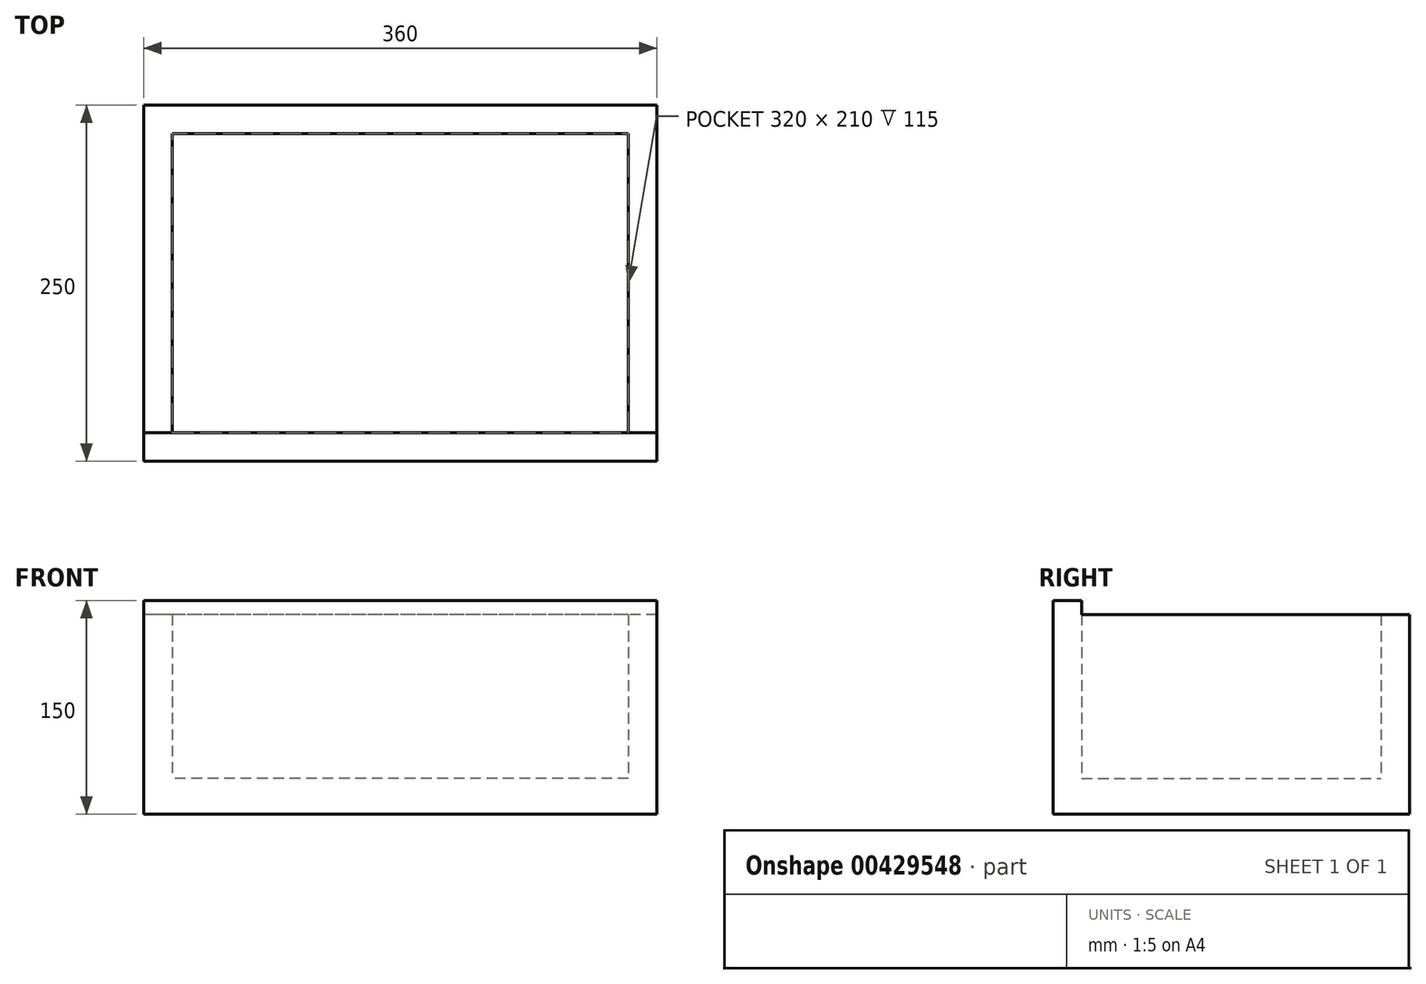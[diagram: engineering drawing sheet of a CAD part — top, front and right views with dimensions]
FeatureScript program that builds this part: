
annotation { "Feature Type Name" : "Feature", "Feature Type Description" : "" }
export const myFeature = defineFeature(function(context is Context, id is Id, definition is map)
    precondition{}
    {
        {
            var Q0;
            Q0=qCreatedBy(makeId("Top.planeOp"),FACE);
            var sketch = newSketch(context, id + "F0", { "sketchPlane" : qUnion([Q0])});
            skLineSegment(sketch, "E0.bottom", {"start": v(180, -125) * mm, "end": v(-180, -125) * mm});
            skLineSegment(sketch, "E0.top", {"start": v(180, 125) * mm, "end": v(-180, 125) * mm});
            skLineSegment(sketch, "E0.left", {"start": v(180, -125) * mm, "end": v(180, 125) * mm});
            skLineSegment(sketch, "E0.right", {"start": v(-180, -125) * mm, "end": v(-180, 125) * mm});
            skPoint(sketch, "E0.middle", {"position": v(0, 0) * mm});
            skLineSegment(sketch, "E1.0", {"start": v(160, -125) * mm, "end": v(160, 125) * mm});
            skLineSegment(sketch, "E2.0", {"start": v(180, 105) * mm, "end": v(-180, 105) * mm});
            skLineSegment(sketch, "E3.0", {"start": v(-160, -125) * mm, "end": v(-160, 125) * mm});
            skLineSegment(sketch, "E4.0", {"start": v(180, -105) * mm, "end": v(-180, -105) * mm});
            skSolve(sketch);
        }
        {
            var Q0;
            {var subQ0=sQuery(id+"F0.wireOp",EDGE,"E0.right");var subQ1=sQuery(id+"F0.wireOp",EDGE,"E0.bottom");var subQ2=makeQuery(id+"F0.imprint","INTERSECT",VERTEX,{"derivedFrom":[subQ1,subQ0]});Q0=makeQuery(id+"F0.imprint","IMPRINT",FACE,{"disambiguationData":[TD([[makeQuery(id+"F0.imprint","IMPRINT",EDGE,{"disambiguationData":[TD([[subQ2,1.0]])],"derivedFrom":subQ1}),-1.0]])]});}
            var Q1;
            {var subQ0=sQuery(id+"F0.wireOp",EDGE,"E1.0");var subQ1=sQuery(id+"F0.wireOp",EDGE,"E0.bottom");var subQ2=makeQuery(id+"F0.imprint","INTERSECT",VERTEX,{"derivedFrom":[subQ1,subQ0]});Q1=makeQuery(id+"F0.imprint","IMPRINT",FACE,{"disambiguationData":[TD([[makeQuery(id+"F0.imprint","IMPRINT",EDGE,{"disambiguationData":[TD([[subQ2,-1.0]])],"derivedFrom":subQ1}),-1.0]])]});}
            var Q2;
            {var subQ0=sQuery(id+"F0.wireOp",EDGE,"E0.left");var subQ1=sQuery(id+"F0.wireOp",EDGE,"E0.bottom");var subQ2=makeQuery(id+"F0.imprint","INTERSECT",VERTEX,{"derivedFrom":[subQ1,subQ0]});Q2=makeQuery(id+"F0.imprint","IMPRINT",FACE,{"disambiguationData":[TD([[makeQuery(id+"F0.imprint","IMPRINT",EDGE,{"disambiguationData":[TD([[subQ2,-1.0]])],"derivedFrom":subQ1}),-1.0]])]});}
            extrude(context, id + "F1", {"entities" : qUnion([Q0, Q1, Q2]), "depth" : 150 * mm});
        }
        {
            var Q0;
            {var subQ0=sQuery(id+"F0.wireOp",EDGE,"E2.0");var subQ1=sQuery(id+"F0.wireOp",EDGE,"E0.right");var subQ2=makeQuery(id+"F0.imprint","INTERSECT",VERTEX,{"derivedFrom":[subQ1,subQ0]});Q0=makeQuery(id+"F0.imprint","IMPRINT",FACE,{"disambiguationData":[TD([[makeQuery(id+"F0.imprint","IMPRINT",EDGE,{"disambiguationData":[TD([[subQ2,1.0]])],"derivedFrom":subQ1}),-1.0]])]});}
            var Q1;
            {var subQ0=sQuery(id+"F0.wireOp",EDGE,"E0.right");var subQ1=sQuery(id+"F0.wireOp",EDGE,"E0.top");var subQ2=makeQuery(id+"F0.imprint","INTERSECT",VERTEX,{"derivedFrom":[subQ1,subQ0]});Q1=makeQuery(id+"F0.imprint","IMPRINT",FACE,{"disambiguationData":[TD([[makeQuery(id+"F0.imprint","IMPRINT",EDGE,{"disambiguationData":[TD([[subQ2,1.0]])],"derivedFrom":subQ1}),1.0]])]});}
            var Q2;
            {var subQ0=sQuery(id+"F0.wireOp",EDGE,"E1.0");var subQ1=sQuery(id+"F0.wireOp",EDGE,"E0.top");var subQ2=makeQuery(id+"F0.imprint","INTERSECT",VERTEX,{"derivedFrom":[subQ1,subQ0]});Q2=makeQuery(id+"F0.imprint","IMPRINT",FACE,{"disambiguationData":[TD([[makeQuery(id+"F0.imprint","IMPRINT",EDGE,{"disambiguationData":[TD([[subQ2,-1.0]])],"derivedFrom":subQ1}),1.0]])]});}
            var Q3;
            {var subQ0=sQuery(id+"F0.wireOp",EDGE,"E0.left");var subQ1=sQuery(id+"F0.wireOp",EDGE,"E0.top");var subQ2=makeQuery(id+"F0.imprint","INTERSECT",VERTEX,{"derivedFrom":[subQ1,subQ0]});Q3=makeQuery(id+"F0.imprint","IMPRINT",FACE,{"disambiguationData":[TD([[makeQuery(id+"F0.imprint","IMPRINT",EDGE,{"disambiguationData":[TD([[subQ2,-1.0]])],"derivedFrom":subQ1}),1.0]])]});}
            var Q4;
            {var subQ0=sQuery(id+"F0.wireOp",EDGE,"E2.0");var subQ1=sQuery(id+"F0.wireOp",EDGE,"E0.left");var subQ2=makeQuery(id+"F0.imprint","INTERSECT",VERTEX,{"derivedFrom":[subQ1,subQ0]});Q4=makeQuery(id+"F0.imprint","IMPRINT",FACE,{"disambiguationData":[TD([[makeQuery(id+"F0.imprint","IMPRINT",EDGE,{"disambiguationData":[TD([[subQ2,1.0]])],"derivedFrom":subQ1}),1.0]])]});}
            extrude(context, id + "F2", {"entities" : qUnion([Q0, Q1, Q2, Q3, Q4]), "operationType" : NewBodyOperationType.ADD, "depth" : 140 * mm});
        }
        {
            var Q0;
            {var subQ0=sQuery(id+"F0.wireOp",EDGE,"E4.0");var subQ1=sQuery(id+"F0.wireOp",EDGE,"E1.0");var subQ2=makeQuery(id+"F0.imprint","INTERSECT",VERTEX,{"derivedFrom":[subQ1,subQ0]});Q0=makeQuery(id+"F0.imprint","IMPRINT",FACE,{"disambiguationData":[TD([[makeQuery(id+"F0.imprint","IMPRINT",EDGE,{"disambiguationData":[TD([[subQ2,-1.0]])],"derivedFrom":subQ1}),1.0]])]});}
            extrude(context, id + "F3", {"entities" : qUnion([Q0]), "operationType" : NewBodyOperationType.ADD, "depth" : 25 * mm});
        }
    });
